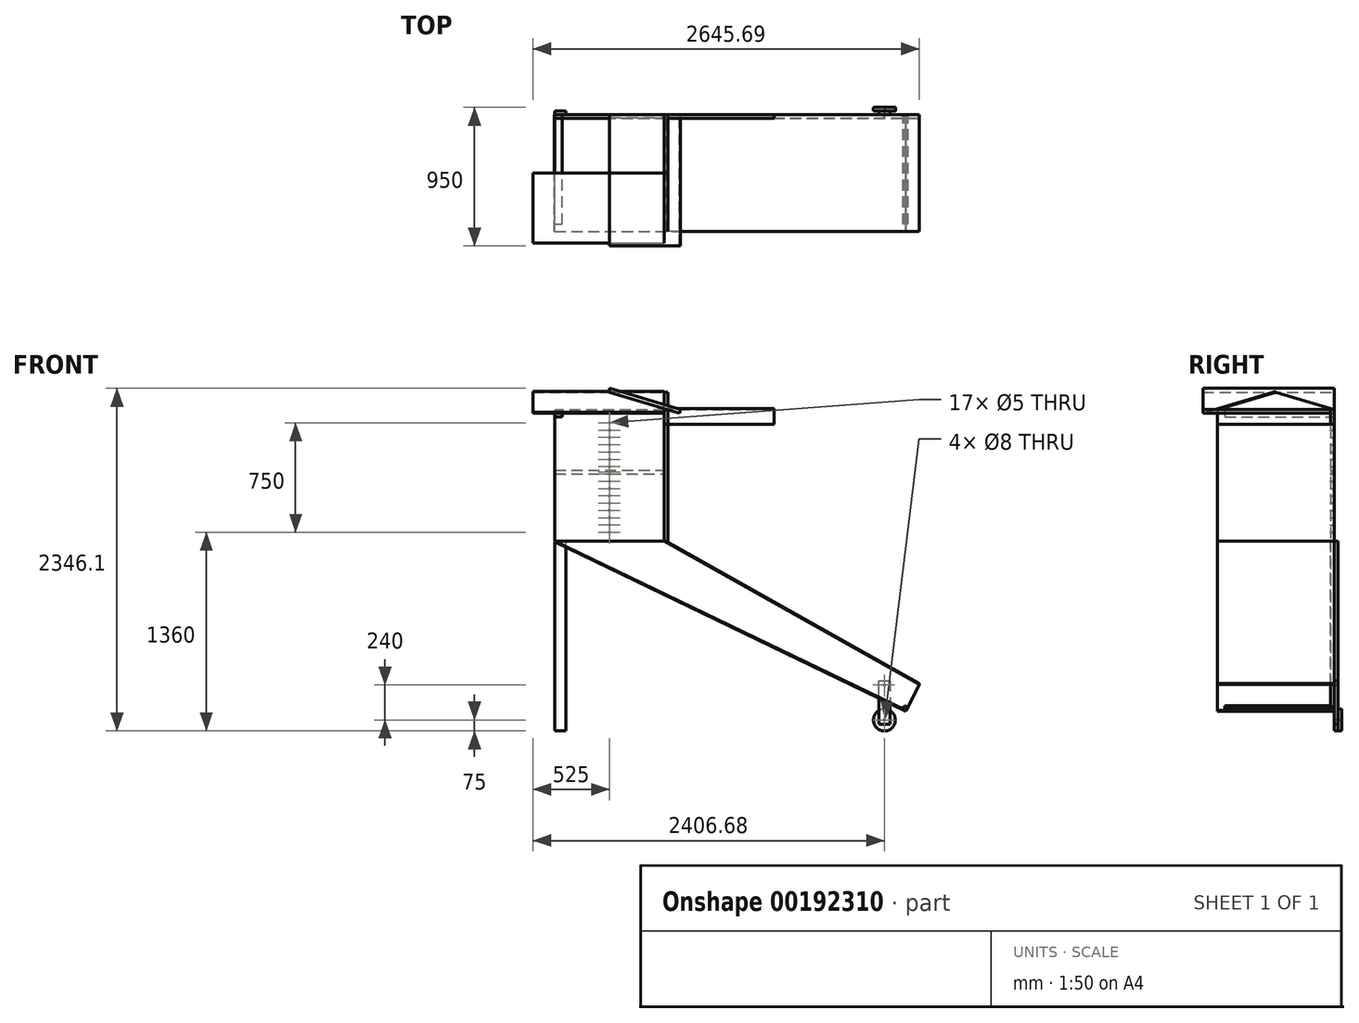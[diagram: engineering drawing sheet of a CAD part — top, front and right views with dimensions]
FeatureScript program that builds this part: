
annotation { "Feature Type Name" : "Feature", "Feature Type Description" : "" }
export const myFeature = defineFeature(function(context is Context, id is Id, definition is map)
    precondition{}
    {
        {
            var Q0;
            Q0=qCreatedBy(makeId("Front.planeOp"),FACE);
            var sketch = newSketch(context, id + "F0", { "sketchPlane" : qUnion([Q0])});
            skLineSegment(sketch, "E0", {"start": v(0, 0) * mm, "end": v(1656.68, -1160.02) * mm, "construction": true});
            skLineSegment(sketch, "E1", {"start": v(1656.68, -1160.02) * mm, "end": v(1743.52, -979.86) * mm});
            skLineSegment(sketch, "E2", {"start": v(1743.52, -979.86) * mm, "end": v(0, 200) * mm, "construction": true});
            skLineSegment(sketch, "E3", {"start": v(0, 200) * mm, "end": v(0, 900) * mm});
            skLineSegment(sketch, "E4", {"start": v(0, 900) * mm, "end": v(-750, 900) * mm});
            skLineSegment(sketch, "E5", {"start": v(-750, 900) * mm, "end": v(-750, 0) * mm});
            skLineSegment(sketch, "E6", {"start": v(-750, 0) * mm, "end": v(0, 0) * mm});
            skLineSegment(sketch, "E7", {"start": v(0, 200) * mm, "end": v(0, 0) * mm});
            skLineSegment(sketch, "E8", {"start": v(0, 200) * mm, "end": v(-750, 200) * mm, "construction": true});
            skLineSegment(sketch, "E9", {"start": v(1656.68, -1160.02) * mm, "end": v(0, -1160.02) * mm, "construction": true});
            skLineSegment(sketch, "E10", {"start": v(-750, 0) * mm, "end": v(1656.68, -1160.02) * mm});
            skLineSegment(sketch, "E11", {"start": v(1743.52, -979.86) * mm, "end": v(0, 0) * mm});
            skSolve(sketch);
        }
        {
            var Q0;
            Q0=makeQuery(id+"F0.imprint","IMPRINT",FACE,{"disambiguationData":[TD([[makeQuery(id+"F0.imprint","IMPRINT",EDGE,{"derivedFrom":sQuery(id+"F0.wireOp",EDGE,"E1")}),1.0]])]});
            extrude(context, id + "F1", {"entities" : qUnion([Q0]), "depth" : 25 * mm});
        }
        {
            var Q0;
            Q0=makeQuery(id+"F0.imprint","IMPRINT",FACE,{"disambiguationData":[TD([[makeQuery(id+"F0.imprint","IMPRINT",EDGE,{"derivedFrom":sQuery(id+"F0.wireOp",EDGE,"E3")}),1.0]])]});
            extrude(context, id + "F2", {"entities" : qUnion([Q0]), "depth" : 25 * mm});
        }
        {
            var Q0;
            Q0=qCreatedBy(makeId("Front.planeOp"),FACE);
            var sketch = newSketch(context, id + "F3", { "sketchPlane" : qUnion([Q0])});
            skPoint(sketch, "E12.0", {"position": v(-750, 900) * mm});
            skLineSegment(sketch, "E13.bottom", {"start": v(-750, 900) * mm, "end": v(-700, 900) * mm});
            skLineSegment(sketch, "E13.top", {"start": v(-750, 850) * mm, "end": v(-700, 850) * mm});
            skLineSegment(sketch, "E13.left", {"start": v(-750, 900) * mm, "end": v(-750, 850) * mm});
            skLineSegment(sketch, "E13.right", {"start": v(-700, 900) * mm, "end": v(-700, 850) * mm});
            skPoint(sketch, "E14.0", {"position": v(1667.54, -1137.5) * mm});
            skLineSegment(sketch, "E15.bottom", {"start": v(1667.54, -1137.5) * mm, "end": v(1645.02, -1126.65) * mm});
            skLineSegment(sketch, "E15.top", {"start": v(1656.68, -1160.02) * mm, "end": v(1634.16, -1149.17) * mm});
            skLineSegment(sketch, "E15.left", {"start": v(1667.54, -1137.5) * mm, "end": v(1656.68, -1160.02) * mm});
            skLineSegment(sketch, "E15.right", {"start": v(1645.02, -1126.65) * mm, "end": v(1634.16, -1149.17) * mm});
            skSolve(sketch);
        }
        {
            var Q0;
            Q0 = qSketchRegion(id + "F3", true);
            extrude(context, id + "F4", {"entities" : qUnion([Q0]), "depth" : 750 * mm});
        }
        {
            var Q0;
            Q0=qCreatedBy(makeId("Front.planeOp"),FACE);
            var sketch = newSketch(context, id + "F5", { "sketchPlane" : qUnion([Q0])});
            skPoint(sketch, "E16.0", {"position": v(0, 900) * mm});
            skPoint(sketch, "E16.1", {"position": v(0, 0) * mm});
            skLineSegment(sketch, "E17", {"start": v(0, 0) * mm, "end": v(0, 900) * mm});
            skLineSegment(sketch, "E18", {"start": v(25, 900) * mm, "end": v(25, 0) * mm});
            skLineSegment(sketch, "E19", {"start": v(25, 0) * mm, "end": v(0, 0) * mm});
            skLineSegment(sketch, "E20", {"start": v(0, 900) * mm, "end": v(25, 900) * mm});
            skSolve(sketch);
        }
        {
            var Q0;
            Q0 = qSketchRegion(id + "F5", true);
            extrude(context, id + "F6", {"entities" : qUnion([Q0]), "depth" : 800 * mm});
        }
        {
            var Q0;
            Q0=qCreatedBy(makeId("Front.planeOp"),FACE);
            var sketch = newSketch(context, id + "F7", { "sketchPlane" : qUnion([Q0])});
            skPoint(sketch, "E21.0", {"position": v(-750, 0) * mm});
            skPoint(sketch, "E22.0", {"position": v(1656.68, -1160.02) * mm});
            skLineSegment(sketch, "E23.0", {"start": v(-750, 0) * mm, "end": v(1656.68, -1160.02) * mm});
            skLineSegment(sketch, "E24.top", {"start": v(-752.17, -4.5) * mm, "end": v(1654.51, -1164.53) * mm});
            skLineSegment(sketch, "E24.left", {"start": v(-750, 0) * mm, "end": v(-752.17, -4.5) * mm});
            skLineSegment(sketch, "E24.right", {"start": v(1656.68, -1160.02) * mm, "end": v(1654.51, -1164.53) * mm});
            skSolve(sketch);
        }
        {
            var Q0;
            Q0 = qSketchRegion(id + "F7", true);
            extrude(context, id + "F8", {"entities" : qUnion([Q0]), "depth" : 800 * mm});
        }
        {
            var Q0;
            Q0=qCreatedBy(makeId("Front.planeOp"),FACE);
            var sketch = newSketch(context, id + "F9", { "sketchPlane" : qUnion([Q0])});
            skLineSegment(sketch, "E25.bottom", {"start": v(-750, 484.95) * mm, "end": v(0, 484.95) * mm});
            skLineSegment(sketch, "E25.top", {"start": v(-750, 459.95) * mm, "end": v(0, 459.95) * mm});
            skLineSegment(sketch, "E25.left", {"start": v(-750, 484.95) * mm, "end": v(-750, 459.95) * mm});
            skLineSegment(sketch, "E25.right", {"start": v(0, 484.95) * mm, "end": v(0, 459.95) * mm});
            skCircle(sketch, "E26", {"center": v(-375, 472.45) * mm, "radius": 2.5 * mm});
            skPoint(sketch, "E26.centerSnap0", {"position": v(-375, 459.95) * mm});
            skPoint(sketch, "E27", {"position": v(-750, 472.45) * mm});
            skSolve(sketch);
        }
        {
            var Q0;
            Q0 = qSketchRegion(id + "F9", true);
            extrude(context, id + "F10", {"entities" : qUnion([Q0]), "depth" : 20 * mm});
        }
        {
            var Q0;
            Q0=qCreatedBy(makeId("Front.planeOp"),FACE);
            var sketch = newSketch(context, id + "F11", { "sketchPlane" : qUnion([Q0])});
            skLineSegment(sketch, "E28", {"start": v(-853.91, 876.33) * mm, "end": v(-375, 1020) * mm, "construction": true});
            skLineSegment(sketch, "E29", {"start": v(-375, 1020) * mm, "end": v(103.91, 876.33) * mm});
            skPoint(sketch, "E30.0", {"position": v(-375, 900) * mm});
            skLineSegment(sketch, "E31", {"start": v(-375, 1020) * mm, "end": v(-375, 1046.1) * mm});
            skLineSegment(sketch, "E32", {"start": v(-375, 1046.1) * mm, "end": v(111.1, 900.27) * mm});
            skLineSegment(sketch, "E33", {"start": v(111.1, 900.27) * mm, "end": v(103.91, 876.33) * mm});
            skPoint(sketch, "E34.0", {"position": v(0, 900) * mm});
            skLineSegment(sketch, "E35", {"start": v(0, 900) * mm, "end": v(25, 900) * mm, "construction": true});
            skPoint(sketch, "E36.0", {"position": v(-750, 900) * mm});
            skLineSegment(sketch, "E37", {"start": v(-750, 900) * mm, "end": v(-775, 900) * mm, "construction": true});
            skSolve(sketch);
        }
        {
            var Q0;
            Q0 = qSketchRegion(id + "F11", true);
            extrude(context, id + "F12", {"entities" : qUnion([Q0]), "depth" : 900 * mm});
        }
        {
            var Q0;
            Q0=qCreatedBy(makeId("Front.planeOp"),FACE);
            var sketch = newSketch(context, id + "F13", { "sketchPlane" : qUnion([Q0])});
            skLineSegment(sketch, "E38.0", {"start": v(25, 0) * mm, "end": v(0, 0) * mm, "construction": true});
            skLineSegment(sketch, "E39.0", {"start": v(1743.52, -979.86) * mm, "end": v(0, 0) * mm});
            skLineSegment(sketch, "E40", {"start": v(1743.52, -979.86) * mm, "end": v(1745.7, -975.36) * mm});
            skLineSegment(sketch, "E41", {"start": v(1745.7, -975.36) * mm, "end": v(10.19, 0) * mm});
            skPoint(sketch, "E41.endSnap0", {"position": v(12.5, 0) * mm});
            skLineSegment(sketch, "E42", {"start": v(10.19, 0) * mm, "end": v(0, 0) * mm});
            skSolve(sketch);
        }
        {
            var Q0;
            Q0 = qSketchRegion(id + "F13", true);
            extrude(context, id + "F14", {"entities" : qUnion([Q0]), "depth" : 800 * mm});
        }
        {
            var Q0;
            Q0=qCreatedBy(makeId("Right.planeOp"),FACE);
            var sketch = newSketch(context, id + "F15", { "sketchPlane" : qUnion([Q0])});
            skLineSegment(sketch, "E43.0", {"start": v(-800, 900) * mm, "end": v(0, 900) * mm, "construction": true});
            skLineSegment(sketch, "E44", {"start": v(-400, 900) * mm, "end": v(-400, 1020) * mm, "construction": true});
            skLineSegment(sketch, "E45", {"start": v(-400, 1020) * mm, "end": v(-878.91, 876.33) * mm});
            skLineSegment(sketch, "E46", {"start": v(-878.91, 876.33) * mm, "end": v(-880.35, 881.12) * mm});
            skLineSegment(sketch, "E47", {"start": v(-880.35, 881.12) * mm, "end": v(-400, 1025.22) * mm});
            skLineSegment(sketch, "E48", {"start": v(-400, 1025.22) * mm, "end": v(-400, 1020) * mm});
            skLineSegment(sketch, "E49", {"start": v(-800, 900) * mm, "end": v(-800, 800) * mm});
            skLineSegment(sketch, "E50", {"start": v(-800, 800) * mm, "end": v(0, 800) * mm});
            skLineSegment(sketch, "E51", {"start": v(0, 800) * mm, "end": v(0, 900) * mm});
            skLineSegment(sketch, "E52", {"start": v(-400, 1020) * mm, "end": v(0, 900) * mm});
            skSolve(sketch);
        }
        {
            var Q0;
            {var subQ1=sQuery(id+"F15.wireOp",EDGE,"E46");Q0=makeQuery(id+"F15.imprint","IMPRINT",FACE,{"disambiguationData":[TD([[makeQuery(id+"F15.imprint","IMPRINT",EDGE,{"derivedFrom":subQ1}),-1.0]])]});}
            extrude(context, id + "F16", {"entities" : qUnion([Q0]), "oppositeDirection" : true, "depth" : 900 * mm});
        }
        {
            var Q0;
            {var subQ1=sQuery(id+"F15.wireOp",EDGE,"E49");Q0=makeQuery(id+"F15.imprint","IMPRINT",FACE,{"disambiguationData":[TD([[makeQuery(id+"F15.imprint","IMPRINT",EDGE,{"derivedFrom":subQ1}),1.0]])]});}
            extrude(context, id + "F17", {"entities" : qUnion([Q0]), "depth" : 25 * mm});
        }
        {
            var Q0;
            Q0=makeQuery(id+"F17.opExtrude","CAP_FACE",FACE,{"disambiguationData":[OSD([sQuery(id+"F15.wireOp",EDGE,"E45"),sQuery(id+"F15.wireOp",EDGE,"E49"),sQuery(id+"F15.wireOp",EDGE,"E50"),sQuery(id+"F15.wireOp",EDGE,"E51"),sQuery(id+"F15.wireOp",EDGE,"E52")])],"isStart":false});
            var sketch = newSketch(context, id + "F18", { "sketchPlane" : qUnion([Q0])});
            skLineSegment(sketch, "E53.0", {"start": v(0, 800) * mm, "end": v(0, 900) * mm});
            skLineSegment(sketch, "E54", {"start": v(0, 900) * mm, "end": v(-25, 907.5) * mm});
            skLineSegment(sketch, "E55", {"start": v(-25, 907.5) * mm, "end": v(-25, 800) * mm});
            skLineSegment(sketch, "E56", {"start": v(-25, 800) * mm, "end": v(0, 800) * mm});
            skSolve(sketch);
        }
        {
            var Q0;
            Q0 = qSketchRegion(id + "F18", true);
            extrude(context, id + "F19", {"entities" : qUnion([Q0]), "depth" : 725 * mm});
        }
        {
            var Q0;
            Q0=qCreatedBy(makeId("Top.planeOp"),FACE);
            cPlane(context, id + "F20", {"entities" : qUnion([Q0]), "cplaneType" : CPlaneType.OFFSET, "offset" : 1300 * mm, "oppositeDirection" : true, "width" : 150 * mm, "height" : 150 * mm});
        }
        {
            var Q0;
            Q0=qCreatedBy(makeId("Front.planeOp"),FACE);
            var sketch = newSketch(context, id + "F21", { "sketchPlane" : qUnion([Q0])});
            skPoint(sketch, "E57.0", {"position": v(-750, 0) * mm});
            skLineSegment(sketch, "E58", {"start": v(-750, 0) * mm, "end": v(-750, -1300) * mm});
            skLineSegment(sketch, "E59", {"start": v(-750, -1300) * mm, "end": v(-675, -1300) * mm});
            skLineSegment(sketch, "E60", {"start": v(-675, -1300) * mm, "end": v(-675, 0) * mm});
            skLineSegment(sketch, "E61", {"start": v(-675, 0) * mm, "end": v(-750, 0) * mm});
            skSolve(sketch);
        }
        {
            var Q0;
            Q0 = qSketchRegion(id + "F21", true);
            extrude(context, id + "F22", {"entities" : qUnion([Q0]), "oppositeDirection" : true, "depth" : 25 * mm});
        }
        {
            var Q0;
            Q0=qCreatedBy(makeId("Front.planeOp"),FACE);
            var sketch = newSketch(context, id + "F23", { "sketchPlane" : qUnion([Q0])});
            skCircle(sketch, "E62", {"center": v(1506.68, -1225) * mm, "radius": 75 * mm, "construction": true});
            skLineSegment(sketch, "E63", {"start": v(1544.18, -1255) * mm, "end": v(1469.18, -1255) * mm});
            skLineSegment(sketch, "E64", {"start": v(1469.18, -1255) * mm, "end": v(1469.18, -955) * mm});
            skLineSegment(sketch, "E65", {"start": v(1469.18, -955) * mm, "end": v(1544.18, -955) * mm});
            skLineSegment(sketch, "E66", {"start": v(1544.18, -955) * mm, "end": v(1544.18, -1255) * mm});
            skLineSegment(sketch, "E67", {"start": v(1544.18, -1255) * mm, "end": v(1506.68, -1225) * mm, "construction": true});
            skLineSegment(sketch, "E68", {"start": v(1469.18, -1255) * mm, "end": v(1506.68, -1225) * mm, "construction": true});
            skCircle(sketch, "E69", {"center": v(1506.68, -1225) * mm, "radius": 4 * mm});
            skSolve(sketch);
        }
        {
            var Q0;
            Q0=makeQuery(id+"F23.imprint","IMPRINT",FACE,{"disambiguationData":[TD([[makeQuery(id+"F23.imprint","IMPRINT",EDGE,{"derivedFrom":sQuery(id+"F23.wireOp",EDGE,"E63")}),-1.0]])]});
            extrude(context, id + "F24", {"entities" : qUnion([Q0]), "oppositeDirection" : true, "depth" : 25 * mm});
        }
        {
            var Q0;
            Q0=makeQuery(id+"F24.opExtrude","CAP_FACE",FACE,{"disambiguationData":[OSD([sQuery(id+"F23.wireOp",EDGE,"E63"),sQuery(id+"F23.wireOp",EDGE,"E64"),sQuery(id+"F23.wireOp",EDGE,"E65"),sQuery(id+"F23.wireOp",EDGE,"E66")])],"isStart":false});
            var sketch = newSketch(context, id + "F25", { "sketchPlane" : qUnion([Q0])});
            skCircle(sketch, "E70.0", {"center": v(-1506.68, -1225) * mm, "radius": 75 * mm});
            skCircle(sketch, "E71.1", {"center": v(-1506.68, -1225) * mm, "radius": 4 * mm});
            skSolve(sketch);
        }
        {
            var Q0;
            Q0 = qSketchRegion(id + "F25", true);
            extrude(context, id + "F26", {"entities" : qUnion([Q0]), "depth" : 25 * mm});
        }
        {
            var Q0;
            Q0=makeQuery(id+"F24.opExtrude","CAP_FACE",FACE,{"disambiguationData":[OSD([sQuery(id+"F23.wireOp",EDGE,"E63"),sQuery(id+"F23.wireOp",EDGE,"E64"),sQuery(id+"F23.wireOp",EDGE,"E65"),sQuery(id+"F23.wireOp",EDGE,"E66"),sQuery(id+"F23.wireOp",EDGE,"E69")])],"isStart":false});
            var sketch = newSketch(context, id + "F27", { "sketchPlane" : qUnion([Q0])});
            skCircle(sketch, "E72", {"center": v(-1506.68, -985) * mm, "radius": 4 * mm});
            skLineSegment(sketch, "E73", {"start": v(-1506.68, -985) * mm, "end": v(-1544.18, -955) * mm, "construction": true});
            skLineSegment(sketch, "E74", {"start": v(-1506.68, -985) * mm, "end": v(-1469.18, -955) * mm, "construction": true});
            skSolve(sketch);
        }
        {
            var Q0;
            Q0 = qSketchRegion(id + "F27", true);
            extrude(context, id + "F28", {"entities" : qUnion([Q0]), "operationType" : NewBodyOperationType.REMOVE, "endBound" : BoundingType.THROUGH_ALL, "oppositeDirection" : true, "depth" : 25 * mm});
        }
        {
            var Q0;
            Q0=makeQuery(id+"F0.imprint","IMPRINT",FACE,{"disambiguationData":[TD([[makeQuery(id+"F0.imprint","IMPRINT",EDGE,{"derivedFrom":sQuery(id+"F0.wireOp",EDGE,"E3")}),1.0]])]});
            var sketch = newSketch(context, id + "F29", { "sketchPlane" : qUnion([Q0])});
            skCircle(sketch, "E75", {"center": v(-375, 60) * mm, "radius": 2.5 * mm});
            skCircle(sketch, "E76.0.1.0", {"center": v(-375, 110) * mm, "radius": 2.5 * mm});
            skCircle(sketch, "E76.0.2.0", {"center": v(-375, 160) * mm, "radius": 2.5 * mm});
            skCircle(sketch, "E76.0.3.0", {"center": v(-375, 210) * mm, "radius": 2.5 * mm});
            skCircle(sketch, "E76.0.4.0", {"center": v(-375, 260) * mm, "radius": 2.5 * mm});
            skCircle(sketch, "E76.0.5.0", {"center": v(-375, 310) * mm, "radius": 2.5 * mm});
            skCircle(sketch, "E76.0.6.0", {"center": v(-375, 360) * mm, "radius": 2.5 * mm});
            skCircle(sketch, "E76.0.7.0", {"center": v(-375, 410) * mm, "radius": 2.5 * mm});
            skCircle(sketch, "E76.0.8.0", {"center": v(-375, 460) * mm, "radius": 2.5 * mm});
            skCircle(sketch, "E76.0.9.0", {"center": v(-375, 510) * mm, "radius": 2.5 * mm});
            skCircle(sketch, "E76.0.10.0", {"center": v(-375, 560) * mm, "radius": 2.5 * mm});
            skCircle(sketch, "E76.0.11.0", {"center": v(-375, 610) * mm, "radius": 2.5 * mm});
            skCircle(sketch, "E76.0.12.0", {"center": v(-375, 660) * mm, "radius": 2.5 * mm});
            skCircle(sketch, "E76.0.13.0", {"center": v(-375, 710) * mm, "radius": 2.5 * mm});
            skLineSegment(sketch, "E76.direction1", {"start": v(-375, 60) * mm, "end": v(-350, 60) * mm, "construction": true});
            skLineSegment(sketch, "E76.direction2", {"start": v(-375, 60) * mm, "end": v(-375, 110) * mm, "construction": true});
            skCircle(sketch, "E77.0.0.14", {"center": v(-375, 760) * mm, "radius": 2.5 * mm});
            skCircle(sketch, "E77.0.0.15", {"center": v(-375, 810) * mm, "radius": 2.5 * mm});
            skSolve(sketch);
        }
        {
            var Q0;
            Q0 = qSketchRegion(id + "F29", true);
            extrude(context, id + "F30", {"entities" : qUnion([Q0]), "operationType" : NewBodyOperationType.REMOVE, "endBound" : BoundingType.THROUGH_ALL, "depth" : 25 * mm});
        }
    });
